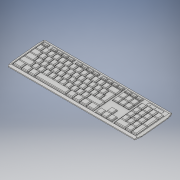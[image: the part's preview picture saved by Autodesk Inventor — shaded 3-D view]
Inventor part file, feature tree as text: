
AUTODESK INVENTOR PART (.ipt)
format: ipt  version: 2017 (Build 210142000, 142)  size: 3,176,448 bytes
history: native  units: in
note: dims shown in document units (in); Inventor stores cm internally (conversion verified against a paired STEP export)
features: other x111, loft x104, extrude x17, sketch x15, mirror x3, plane x2, fillet x1
ambient origin geometry x8: Origin, YZ Plane, XZ Plane, XY Plane, X Axis, Y Axis, Z Axis, Center Point
bodies: Solid4 (feature_tree)
feature tree (253):
  other  "key board"
  extrude  "key board to cut from"  Depth=0.4271in
  extrude  "curve top and bottom"  Depth=0.0938in
  extrude  "curve corners"  Depth=0.3125in
  other  "side curve workplane"
  extrude  "right curve edge"  Depth=0.0053in
  mirror  "mirror plane"
  mirror  "mirror right edge"
  other  "right curve workplane"
  extrude  "right curve diaganal"  Depth=0.0163in
  mirror  "mirror curve right"
  extrude  "leftover from diaganal and right curve"  Depth=0.0238in
  extrude  "back curve corner"  Depth=0.009in
  extrude  "ramp for keys"  Depth=0.0011in
  other  "ramp flushing plane"
  extrude  "ramp flushed"  Depth=0.015in
  extrude  "ramp random extion"  Depth=0.0153in
  plane  "Work Plane9"
  extrude  "top side curve"  Depth=1.0in TaperAngle=0.0deg
  extrude  "key slots"  Depth=0.0208in
  other  "keys workplane"
  extrude  "bottom of keys"  Depth=0.0036in
  plane  "Work Plane10"
  sketch  "Sketch23"  dims[d45=90.0deg d55=0.0208in]
  extrude  "Caps lock and Num Lock light indicators cut out"  Depth=1.0in TaperAngle=0.0deg
  sketch  "Sketch25"  dims[d58=0.7136in d67=1.0in d68=0.0in]
  extrude  "light indicators cut out"  Depth=0.0036in
  extrude  "light indicators join"  Depth=0.0005in TaperAngle=0.0deg
  loft  "~ key"
  loft  "1! key"
  loft  "2@ key"
  loft  "3# key"
  loft  "4$ key"
  loft  "5% key"
  loft  "6^ key"
  loft  "7& key"
  loft  "8* key"
  loft  "9( key"
  loft  "0) key"
  loft  "-_ key"
  loft  "=+ key"
  loft  "Q key"
  loft  "W key"
  loft  "E key"
  loft  "R key"
  loft  "T key"
  loft  "Y key"
  loft  "U key"
  loft  "I key"
  loft  "O key"
  loft  "P key"
  loft  "[{ key"
  loft  "]} key"
  loft  "\| key"
  loft  "'" key"
  loft  ";: key"
  loft  "L key"
  loft  "K key"
  loft  "J key"
  loft  "H key"
  loft  "G key"
  loft  "F key"
  loft  "D key"
  loft  "S key"
  loft  "A key"
  loft  "Z key"
  loft  "X key"
  loft  "C key"
  loft  "V key"
  loft  "B key"
  loft  "N key"
  loft  "M key"
  loft  ",< key"
  loft  ".> key"
  loft  "/? key"
  loft  "Tab  key"
  loft  "Caps Lock  key"
  loft  "Left Shift key"
  loft  "Left Ctrl key"
  loft  "Left FN  key"
  loft  "Left Alt"
  loft  "space bar key"
  loft  "Right Alt  key"
  loft  "Windows  key"
  loft  "Menu  key"
  loft  "Right Ctrl  key"
  loft  "Right Shift  key"
  loft  "Enter  key"
  loft  "Backspace  key"
  loft  "Esc  key"
  loft  "F1  key"
  loft  "F2  key"
  loft  "F3  key"
  loft  "F4  key"
  loft  "F5  key"
  loft  "F6 key"
  loft  "F7 key"
  loft  "F8 key"
  loft  "F9 key"
  loft  "F10  key"
  loft  "F11  key"
  loft  "F12  key"
  loft  "Print Screen  key"
  loft  "Scroll Lock  key"
  loft  "Pause Break  key"
  loft  "Insert  key"
  loft  "Delete  key"
  loft  "End  key"
  loft  "Home  key"
  loft  "Page UP  key"
  loft  "Page Down  key"
  loft  "Up Arrow  key"
  loft  "Left Arrow  key"
  loft  "Down Arrow  key"
  loft  "Right Arrow  key"
  loft  "Num Lock  key"
  loft  "Num /  key"
  loft  "Num *  key"
  loft  "Num -  key"
  loft  "Num +  key"
  loft  "Num Enter  key"
  loft  "Num .  key"
  loft  "Num 1  key"
  loft  "Num 2  key"
  loft  "Num 3  key"
  loft  "Num 4  key"
  loft  "Num 5  key"
  extrude  "little knobs for blind"  Depth=0.1063in
  fillet  "Fillet little knobs"  Radius=0.0041in
  loft  "Num 6  key"
  loft  "Num 7  key"
  loft  "Num 8  key"
  loft  "Num 9  key"
  loft  "Num 0  key"
  other  "put in middle of terminal"
  other  "middle of the key board front to back"
  sketch  "Sketch3"  dims[d12=1.4896in d13=0.4271in]
  sketch  "Sketch4"  dims[d14=0.0749in d15=0.0in d16=0.0938in]
  sketch  "Sketch5"  dims[d17=0.032in d18=0.3125in]
  sketch  "Sketch6"  dims[d19=0.0053in d20=0.0053in]
  sketch  "Sketch8"  dims[d22=0.0036in d23=0.0163in]
  sketch  "Sketch15"  dims[d25=0.0238in d29=0.0238in]
  sketch  "Sketch16"  dims[d30=0.032in d32=0.009in]
  sketch  "Sketch18"  dims[d33=0.0092in d34=0.0011in]
  sketch  "Sketch19"  dims[d36=1.0in d37=0.0in d39=0.015in]
  sketch  "Sketch21"  dims[d40=0.0666in d41=0.0153in]
  sketch  "Sketch22"  dims[d42=0.0621in d43=1.0in d44=0.0in]
  other  "Edges1"
  other  "Edges2"
  other  "Edges3"
  other  "Edges4"
  other  "Edges5"
  other  "Edges6"
  other  "Edges7"
  other  "Edges8"
  other  "Edges9"
  other  "Edges10"
  other  "Edges11"
  other  "Edges12"
  other  "Edges13"
  other  "Edges14"
  other  "Edges15"
  other  "Edges16"
  other  "Edges17"
  other  "Edges18"
  other  "Edges19"
  other  "Edges20"
  other  "Edges21"
  other  "Edges22"
  other  "Edges23"
  other  "Edges24"
  other  "Edges25"
  other  "Edges26"
  other  "Edges27"
  other  "Edges28"
  other  "Edges29"
  other  "Edges30"
  other  "Edges31"
  other  "Edges32"
  other  "Edges33"
  other  "Edges34"
  other  "Edges35"
  other  "Edges36"
  other  "Edges37"
  other  "Edges38"
  other  "Edges39"
  other  "Edges40"
  other  "Edges41"
  other  "Edges42"
  other  "Edges43"
  other  "Edges44"
  other  "Edges45"
  other  "Edges46"
  other  "Edges47"
  other  "Edges48"
  other  "Edges49"
  other  "Edges50"
  other  "Edges51"
  other  "Edges52"
  other  "Edges53"
  other  "Edges54"
  other  "Edges55"
  other  "Edges56"
  other  "Edges57"
  other  "Edges58"
  other  "Edges59"
  other  "Edges60"
  other  "Edges61"
  other  "Edges62"
  other  "Edges63"
  other  "Edges64"
  other  "Edges65"
  other  "Edges66"
  other  "Edges67"
  other  "Edges68"
  other  "Edges69"
  other  "Edges70"
  other  "Edges71"
  other  "Edges72"
  other  "Edges73"
  other  "Edges74"
  other  "Edges75"
  other  "Edges76"
  other  "Edges77"
  other  "Edges78"
  other  "Edges79"
  other  "Edges80"
  other  "Edges81"
  other  "Edges82"
  other  "Edges83"
  other  "Edges84"
  other  "Edges85"
  other  "Edges86"
  other  "Edges87"
  other  "Edges88"
  other  "Edges89"
  other  "Edges90"
  other  "Edges91"
  other  "Edges92"
  other  "Edges93"
  other  "Edges94"
  other  "Edges95"
  other  "Edges96"
  other  "Edges97"
  other  "Edges98"
  other  "Edges99"
  other  "Edges100"
  other  "Edges101"
  other  "Edges102"
  other  "Edges103"
  other  "Edges104"
  sketch  "Sketch24"  dims[d56=0.0053in d57=0.0036in]
  sketch  "Sketch26"  dims[d73=0.0053in d74=0.0036in d76=1.0in d77=0.0in d78=1.0in d79=0.0in d81=0.0058in d82=0.0058in d90=0.0307in d91=0.0307in d94=0.017in d95=0.0653in d96=0.0653in d97=0.0653in d98=0.0653in d99=0.0653in d100=0.017in d101=0.1958in d102=0.1305in d104=0.3262in d106=0.0746in d108=0.0083in d109=0.261in d111=0.0262in d112=0.261in d113=0.0262in d114=0.261in d115=0.02in d116=0.0in d117=0.0083in d118=0.0592in d119=0.0592in d120=0.0592in d121=0.0592in d122=0.0592in d123=0.0592in d124=0.0592in d125=0.0592in d126=0.0592in d127=0.0592in d128=0.0592in d129=0.0592in d130=0.0592in d131=0.0592in d132=0.0041in d133=0.0041in d134=0.0041in d135=0.0041in d136=0.0041in d137=0.0041in d138=0.0041in d139=0.0041in d146=0.0592in d147=0.0592in d148=0.0592in d149=0.0592in d150=0.0592in d151=0.0592in d152=0.0592in d153=0.0592in d154=0.0592in d155=0.0592in d156=0.0592in d157=0.0592in d160=0.0041in d161=0.0041in d162=0.0041in d163=0.0041in d164=0.0041in d166=0.0041in d167=0.0041in d172=0.0041in d173=0.032in d174=0.017in d175=1.0in d176=0.0in d177=0.066in d178=0.066in d179=0.0686in d180=0.0686in d183=90.0deg d184=1.0in d185=0.0in d186=0.0328in d187=0.0031in d188=0.0031in d189=0.063in d190=0.0328in d191=0.0031in d192=0.0031in d193=0.063in d194=1.0in d195=0.0in d196=0.0041in d197=0.1095in d198=0.0041in d199=0.0041in d200=0.0041in d201=0.0041in d202=0.0041in d203=0.0041in d204=0.0041in d205=0.0592in d206=0.0592in d207=0.0592in d208=0.0592in d209=0.0041in d210=0.0041in d213=0.0304in d214=90.0deg d215=0.0091in d216=0.0249in d217=0.0091in d218=0.0249in d219=1.0in d220=0.0in d222=0.0041in d226=0.0592in d227=0.0592in d228=0.0592in d229=0.0592in d230=0.0041in d231=0.0041in d232=0.0041in d233=0.0041in d234=0.0592in d235=0.0041in d236=0.0041in d237=0.0041in d238=0.0592in d239=0.0592in d240=0.0592in d241=0.0592in d242=0.0041in d243=0.0041in d244=0.0041in d248=0.0592in d249=0.0041in d250=0.0041in d251=0.0041in d252=0.0041in d253=0.0041in d254=0.1958in d255=0.017in d256=0.0592in d257=0.0592in d258=0.0592in d260=0.0041in d261=0.0041in d263=0.0592in d264=0.0041in d265=0.0041in d267=0.0592in d268=0.0592in d269=0.0592in d270=0.0592in d271=0.0592in d272=0.0592in d273=0.0592in d274=0.0592in d275=0.0592in d276=0.0592in d277=0.0592in d278=0.0592in d279=0.0592in d280=0.0592in d281=0.0041in d282=0.0041in d283=0.0041in d284=0.0041in d285=0.0041in d286=0.0041in d287=0.0592in d288=0.0592in d289=0.0592in d290=0.0592in d291=0.0592in d292=0.0592in d293=0.0592in d294=0.0592in d295=0.0592in d296=0.0592in d297=0.0041in d298=0.0041in d299=0.0041in d300=0.0041in d301=0.0041in d302=0.0041in d303=0.0041in d304=0.0592in d305=0.0041in d306=0.0041in d307=0.0902in d308=0.0592in d310=0.0041in d311=0.0592in d312=0.1063in d313=0.0041in d314=0.0592in d315=0.0592in d316=0.0592in d317=0.0592in d318=0.0592in d319=0.0592in d320=0.0592in d321=0.0592in d322=0.0592in d323=0.0592in d324=0.0592in d325=0.0592in d326=0.0592in d327=0.0592in d328=0.0041in d329=0.0041in d330=0.0041in d331=0.0041in d332=0.0041in d333=0.0041in d334=0.0592in d335=0.0592in d336=0.0592in d337=0.0592in d338=0.0592in d339=0.0592in d340=0.0592in d341=0.0592in d342=0.0592in d343=0.0592in d344=0.0041in d345=0.0041in d346=0.0041in d347=0.0041in d348=0.0041in d349=0.0592in d350=0.0041in d351=0.0041in d352=0.0041in d353=0.0041in d354=0.0592in d355=0.0592in d356=0.0592in d357=0.0592in d358=0.0592in d359=0.0592in d360=0.0592in d361=0.0592in d362=0.0592in d363=0.0592in d364=0.0592in d365=0.0592in d366=0.0592in d367=0.0592in d368=0.0041in d369=0.0041in d370=0.0041in d371=0.0041in d372=0.0041in d373=0.0041in d374=0.0592in d375=0.0592in d376=0.0592in d377=0.0592in d378=0.0592in d379=0.0592in d380=0.0041in d381=0.0041in d382=0.0041in d383=0.0592in d384=0.0041in d385=0.0041in d386=0.0592in d387=0.0041in d388=0.1355in d389=0.0041in d392=0.0041in d393=0.0592in d394=0.0899in d395=0.0041in d396=0.0041in d397=0.0041in d398=0.0041in d399=0.0041in d400=0.0041in d401=0.0747in d402=0.0747in d403=0.3529in d404=0.0743in d405=0.0755in d406=0.0041in d407=0.0041in d408=0.0747in d410=0.0592in d411=0.0592in d412=0.0592in d413=0.0592in d414=0.0041in d415=0.0592in d416=0.0041in d417=0.0592in d418=0.0592in d419=0.0592in d420=0.0592in d421=0.0041in d422=0.0592in d423=0.0041in d424=0.0592in d425=0.0592in d426=0.0592in d427=0.0592in d428=0.0041in d429=0.0592in d430=0.0041in d431=0.0592in d432=0.0592in d433=0.0592in d434=0.0592in d435=0.0041in d436=0.0592in d437=0.0041in d438=0.0592in d439=0.0592in d440=0.0592in d441=0.0592in d442=0.0041in d443=0.0592in d444=0.0041in d445=0.0592in d446=0.0592in d447=0.0592in d448=0.0592in d449=0.0041in d450=0.0592in d451=0.0041in d452=0.0592in d453=0.0592in d454=0.0592in d455=0.0592in d456=0.0041in d457=0.0592in d458=0.0041in d459=0.0592in d460=0.0592in d461=0.0592in d462=0.0592in d463=0.0041in d464=0.0592in d465=0.0041in d466=0.0041in d467=0.0041in d468=0.0041in d469=0.0041in d470=0.0041in d471=0.0041in d472=0.0041in d473=0.0041in d474=0.0041in d475=0.0041in d476=0.0041in d477=0.0592in d478=0.0592in d479=0.0592in d480=0.0592in d481=0.0592in d482=0.0592in d483=0.0592in d484=0.0592in d485=0.0592in d486=0.0592in d487=0.0592in d488=0.0592in d489=0.0041in d490=0.0041in d491=0.0041in d492=0.0041in d495=0.032in d496=0.0592in d497=0.0592in d498=0.0592in d499=0.0592in d500=0.0592in d501=0.0592in d502=0.0041in d503=0.0041in d504=0.0592in d505=0.0592in d506=0.0592in d507=0.0592in d508=0.0592in d509=0.0592in d510=0.0041in d512=0.0208in d513=0.0091in d514=1.0in d515=0.0in d516=0.0592in d517=0.0592in d518=0.0592in d519=0.0592in d520=0.0592in d522=0.0592in d523=0.0592in d525=0.0592in d526=0.0592in d527=0.0592in d528=0.0592in d530=0.0592in d531=0.0592in d533=0.0592in d534=0.0592in d535=0.0592in d536=0.0592in d538=0.0592in d540=0.0134in d541=0.0in d542=0.0083in d901=0.0246in d905=0.0271in d906=0.021in d909=0.0246in d910=0.0271in d911=0.021in d912=0.0592in d1093=0.0246in d1094=0.0271in d1095=0.021in d1096=0.0592in d1097=0.0246in d1098=0.0271in d1099=0.021in d1100=0.0592in d1101=0.0246in d1102=0.0271in d1103=0.021in d1104=0.0592in d1105=0.0246in d1106=0.0271in d1107=0.021in d1108=0.0592in d1109=0.0246in d1110=0.0271in d1111=0.021in d1112=0.0592in d1113=0.0246in d1114=0.0271in d1115=0.021in d1116=0.0592in d1117=0.0246in d1118=0.0271in d1119=0.021in d1120=0.0592in d1121=0.0246in d1122=0.0271in d1123=0.021in d1124=0.0592in d1125=0.0246in d1126=0.0271in d1127=0.021in d1128=0.0592in d1129=0.0246in d1130=0.0271in d1131=0.021in d1132=0.0592in d1133=0.0246in d1134=0.0271in d1135=0.021in d1136=0.0592in d1137=0.0246in d1138=0.0271in d1139=0.021in d1140=0.0592in d1141=0.0246in d1142=0.0271in d1143=0.021in d1144=0.0592in d1145=0.0246in d1146=0.0271in d1147=0.021in d1148=0.0592in d1149=0.0246in d1150=0.0271in d1151=0.021in d1152=0.0592in d1153=0.0246in d1154=0.0271in d1155=0.021in d1156=0.0592in d1157=0.0246in d1158=0.0271in d1159=0.021in d1160=0.0592in d1161=0.0246in d1162=0.0271in d1163=0.021in d1164=0.0592in d1165=0.0246in d1166=0.0271in d1167=0.021in d1168=0.0592in d1169=0.0246in d1170=0.0271in d1171=0.021in d1172=0.0592in d1173=0.0246in d1174=0.0271in d1175=0.021in d1176=0.0592in d1177=0.0246in d1178=0.0271in d1179=0.021in d1180=0.0592in d1181=0.0246in d1182=0.0271in d1183=0.021in d1184=0.0592in d1185=0.0246in d1186=0.0271in d1187=0.021in d1188=0.0592in d1189=0.0246in d1190=0.0271in d1191=0.021in d1192=0.0592in d1193=0.0246in d1194=0.0271in d1195=0.021in d1196=0.0592in d1197=0.0246in d1198=0.0271in d1199=0.021in d1200=0.0592in d1201=0.0246in d1202=0.0271in d1203=0.021in d1204=0.0592in d1205=0.0246in d1206=0.0271in d1207=0.021in d1208=0.0592in d1209=0.0246in d1210=0.0271in d1211=0.021in d1212=0.0592in d1213=0.0246in d1214=0.0271in d1215=0.021in d1216=0.0592in d1217=0.0246in d1218=0.0271in d1219=0.021in d1220=0.0592in d1221=0.0246in d1222=0.0271in d1223=0.021in d1224=0.0592in d1225=0.0246in d1226=0.0271in d1227=0.021in d1228=0.0592in d1229=0.0246in d1230=0.0271in d1231=0.021in d1232=0.0592in d1233=0.0246in d1234=0.0271in d1235=0.021in d1236=0.0592in d1237=0.0246in d1238=0.0271in d1239=0.021in d1240=0.0592in d1241=0.0246in d1242=0.0271in d1243=0.021in d1244=0.0592in d1245=0.0246in d1246=0.0271in d1247=0.021in d1248=0.0592in d1249=0.0246in d1250=0.0271in d1251=0.021in d1252=0.0592in d1253=0.0246in d1254=0.0271in d1255=0.021in d1256=0.0592in d1257=0.0246in d1258=0.0271in d1259=0.021in d1260=0.0592in d1261=0.0246in d1262=0.0271in d1263=0.021in d1264=0.0592in d1265=0.0246in d1266=0.0271in d1267=0.021in d1268=0.0592in d1269=0.0246in d1270=0.0271in d1271=0.021in d1272=0.0592in d1273=0.0in d1274=90.0deg d1275=0.0in d1276=90.0deg d1277=0.0in d1278=90.0deg d1279=0.0in d1280=90.0deg d1281=0.0in d1282=90.0deg d1283=0.0in d1284=90.0deg d1285=0.0in d1286=90.0deg d1287=0.0in d1288=90.0deg d1289=0.0in d1290=90.0deg d1291=0.0in d1292=90.0deg d1293=0.0in d1294=90.0deg d1295=0.0in d1296=90.0deg d1297=0.0in d1298=90.0deg d1299=0.0in d1300=90.0deg d1301=0.0in d1302=90.0deg d1303=0.0in d1304=90.0deg d1305=0.0in d1306=90.0deg d1307=0.0in d1308=90.0deg d1309=0.0in d1310=90.0deg d1311=0.0in d1312=90.0deg d1313=0.0in d1314=90.0deg d1315=0.0in d1316=90.0deg d1317=0.0in d1318=90.0deg d1319=0.0in d1320=90.0deg d1321=0.0in d1322=90.0deg d1323=0.0in d1324=90.0deg d1325=0.0in d1326=90.0deg d1327=0.0in d1328=90.0deg d1329=0.0in d1330=90.0deg d1331=0.0in d1332=90.0deg d1333=0.0in d1334=90.0deg d1335=0.0in d1336=90.0deg d1337=0.0in d1338=90.0deg d1339=0.0in d1340=90.0deg d1341=0.0in d1342=90.0deg d1343=0.0in d1344=90.0deg d1345=0.0in d1346=90.0deg d1347=0.0in d1348=90.0deg d1349=0.0in d1350=90.0deg d1351=0.0in d1352=90.0deg d1353=0.0in d1354=90.0deg d1355=0.0in d1356=90.0deg d1357=0.0in d1358=90.0deg d1359=0.0in d1360=90.0deg d1361=0.0in d1362=90.0deg d1363=0.0in d1364=90.0deg d1365=0.0in d1366=90.0deg d1367=0.0in d1368=90.0deg d1369=0.0in d1370=90.0deg d1371=0.0in d1372=90.0deg d1373=0.0in d1374=90.0deg d1375=0.0in d1376=90.0deg d1377=0.0in d1378=90.0deg d1379=0.0in d1380=90.0deg d1381=0.0in d1382=90.0deg d1383=0.0in d1384=90.0deg d1385=0.0in d1386=90.0deg d1387=0.0in d1388=90.0deg d1389=0.0in d1390=90.0deg d1391=0.0in d1392=90.0deg d1393=0.0in d1394=90.0deg d1395=0.0in d1396=90.0deg d1397=0.0in d1398=90.0deg d1399=0.0in d1400=90.0deg d1401=0.0in d1402=90.0deg d1403=0.0in d1404=90.0deg d1405=0.0in d1406=90.0deg d1407=0.0in d1408=90.0deg d1409=0.0in d1410=90.0deg d1411=0.0in d1412=90.0deg d1413=0.0in d1414=90.0deg d1415=0.0in d1416=90.0deg d1417=0.0in d1418=90.0deg d1419=0.0in d1420=90.0deg d1421=0.0in d1422=90.0deg d1423=0.0in d1424=90.0deg d1425=0.0in d1426=90.0deg d1427=0.0in d1428=90.0deg d1429=0.0in d1430=90.0deg d1431=0.0in d1432=90.0deg d1433=0.0in d1434=90.0deg d1435=0.0in d1436=90.0deg d1437=0.0in d1438=90.0deg d1439=0.0in d1440=90.0deg d1441=0.0in d1442=90.0deg d1443=0.0in d1444=90.0deg d1445=0.0in d1446=90.0deg d1447=0.0in d1448=90.0deg d1449=0.0in d1450=90.0deg d1451=0.0in d1452=90.0deg d1453=0.0in d1454=90.0deg d1455=0.0in d1456=90.0deg d1457=0.0in d1458=90.0deg d1459=0.0in d1460=90.0deg d1463=0.0246in d1464=0.0271in d1465=0.0365in d1466=0.0592in d1467=0.0246in d1468=0.0271in d1469=0.0445in d1470=0.0592in d1471=0.0902in d1473=0.0246in d1474=0.0271in d1475=0.0591in d1476=0.0592in d1477=0.1063in d1479=0.0246in d1480=0.0271in d1481=0.0461in d1482=0.0592in d1484=0.0246in d1485=0.0271in d1486=0.0363in d1487=0.0592in d1488=0.1355in d1489=0.0246in d1490=0.0271in d1491=0.0287in d1492=0.0592in d1493=0.0899in d1494=0.0246in d1495=0.0271in d1496=0.0288in d1497=0.0592in d1498=0.0899in d1499=0.0246in d1500=0.0271in d1501=0.1678in d1502=0.0592in d1503=0.0899in d1504=0.0246in d1505=0.0271in d1506=0.0285in d1507=0.0592in d1508=0.0899in d1509=0.0246in d1510=0.0271in d1511=0.0291in d1512=0.0592in d1513=0.0899in d1514=0.0246in d1515=0.0271in d1516=0.0288in d1517=0.0592in d1518=0.0899in d1519=0.0246in d1520=0.0271in d1521=0.0348in d1522=0.0592in d1523=0.0899in d1524=0.0246in d1525=0.0271in d1526=0.0713in d1527=0.0592in d1528=0.0899in d1529=0.0869in d1530=0.1598in d1532=0.0271in d1533=0.0306in d1534=0.0592in d1535=0.0246in d1538=0.0592in d1539=0.0785in d1540=0.0624in d1541=0.0226in d1542=0.0in d1543=90.0deg d1544=0.0in d1545=90.0deg d1546=0.0in d1547=90.0deg d1548=0.0in d1549=90.0deg d1550=0.0in d1551=90.0deg d1552=0.0in d1553=90.0deg d1554=0.0in d1555=90.0deg d1556=0.0in d1557=90.0deg d1558=0.0in d1559=90.0deg d1560=0.0in d1561=90.0deg d1562=0.0in d1563=90.0deg d1564=0.0in d1565=90.0deg d1566=0.0in d1567=90.0deg d1568=0.0in d1569=90.0deg d1570=0.0in d1571=90.0deg d1572=0.0in d1573=90.0deg d1574=0.0in d1575=90.0deg d1576=0.0in d1577=90.0deg d1578=0.0in d1579=90.0deg d1580=0.0in d1581=90.0deg d1582=0.0in d1583=90.0deg d1584=0.0in d1585=90.0deg d1586=0.0in d1587=90.0deg d1588=0.0in d1589=90.0deg d1590=0.0in d1591=90.0deg d1592=0.0in d1593=90.0deg d1594=0.0in d1595=90.0deg d1596=0.0in d1597=90.0deg d1598=0.0664in d1599=0.0251in d1602=0.0101in d1603=0.0076in d1604=0.0246in d1605=0.0101in d1606=0.0076in d1607=0.0246in d1608=0.0251in d1609=0.0664in d1610=0.0101in d1611=0.0076in d1612=0.0246in d1613=0.0251in d1614=0.0664in d1615=0.0101in d1616=0.0076in d1617=0.0246in d1618=0.0251in d1619=0.0664in d1620=0.0101in d1621=0.0076in d1622=0.0246in d1623=0.0251in d1624=0.0664in d1625=0.0101in d1626=0.0076in d1627=0.0246in d1628=0.0251in d1629=0.0664in d1630=0.0101in d1631=0.0076in d1632=0.0246in d1633=0.0251in d1634=0.0664in d1635=0.0101in d1636=0.0076in d1637=0.0246in d1638=0.0251in d1639=0.0664in d1640=0.0101in d1641=0.0076in d1642=0.0246in d1643=0.0251in d1644=0.0664in d1645=0.0101in d1646=0.0076in d1647=0.0246in d1648=0.0251in d1649=0.0664in d1650=0.0101in d1651=0.0076in d1652=0.0246in d1653=0.0251in d1654=0.0664in d1655=0.0101in d1656=0.0076in d1657=0.0246in d1658=0.0251in d1659=0.0664in d1660=0.0101in d1661=0.0076in d1662=0.0246in d1663=0.0251in d1664=0.0664in d1665=0.0101in d1666=0.0076in d1667=0.0246in d1668=0.0251in d1669=0.0664in d1670=0.0101in d1671=0.0076in d1672=0.0246in d1673=0.0251in d1674=0.0664in d1675=0.0101in d1676=0.0076in d1677=0.0246in d1678=0.0251in d1679=0.0664in d1680=0.0in d1681=90.0deg d1682=0.0in d1683=90.0deg d1684=0.0in d1685=90.0deg d1686=0.0in d1687=90.0deg d1688=0.0in d1689=90.0deg d1690=0.0in d1691=90.0deg d1692=0.0in d1693=90.0deg d1694=0.0in d1695=90.0deg d1696=0.0in d1697=90.0deg d1698=0.0in d1699=90.0deg d1700=0.0in d1701=90.0deg d1702=0.0in d1703=90.0deg d1704=0.0in d1705=90.0deg d1706=0.0in d1707=90.0deg d1708=0.0in d1709=90.0deg d1710=0.0in d1711=90.0deg d1712=0.0in d1713=90.0deg d1714=0.0in d1715=90.0deg d1716=0.0in d1717=90.0deg d1718=0.0in d1719=90.0deg d1720=0.0in d1721=90.0deg d1722=0.0in d1723=90.0deg d1724=0.0in d1725=90.0deg d1726=0.0in d1727=90.0deg d1728=0.0in d1729=90.0deg d1730=0.0in d1731=90.0deg d1732=0.0in d1733=90.0deg d1734=0.0in d1735=90.0deg d1736=0.0in d1737=90.0deg d1738=0.0in d1739=90.0deg d1740=0.0in d1741=90.0deg d1742=0.0in d1743=90.0deg d1744=0.0271in d1745=0.0246in d1746=0.0246in d1747=0.0251in d1748=0.0664in d1749=0.0271in d1750=0.0246in d1751=0.0246in d1752=0.0251in d1753=0.0664in d1754=0.0271in d1755=0.0246in d1756=0.0246in d1757=0.0251in d1758=0.0664in d1759=0.0271in d1760=0.0246in d1761=0.0246in d1762=0.0251in d1763=0.0664in d1764=0.0271in d1765=0.0246in d1766=0.0246in d1767=0.0251in d1768=0.0664in d1769=0.0271in d1770=0.0246in d1771=0.0246in d1772=0.0251in d1773=0.0664in d1774=0.0271in d1775=0.0246in d1776=0.0246in d1777=0.0592in d1778=0.0664in d1779=0.0592in d1780=0.0271in d1781=0.0246in d1782=0.0246in d1783=0.0592in d1784=0.0664in d1785=0.0592in d1792=0.0271in d1793=0.0246in d1794=0.0246in d1795=0.0592in d1796=0.0664in d1797=0.0592in d1798=0.0271in d1799=0.0246in d1800=0.021in d1801=0.0592in d1802=0.0664in d1803=0.0592in d1804=0.0271in d1805=0.0246in d1806=0.021in d1807=0.0592in d1808=0.0664in d1809=0.0592in d1810=0.0271in d1811=0.0246in d1812=0.021in d1813=0.0592in d1814=0.0664in d1815=0.0592in d1816=0.0271in d1817=0.0246in d1818=0.021in d1819=0.0592in d1820=0.0664in d1821=0.0592in d1822=0.0271in d1823=0.0246in d1824=0.021in d1825=0.0592in d1826=0.0664in d1827=0.0592in d1828=0.0271in d1829=0.0246in d1830=0.021in d1831=0.0592in d1832=0.0664in d1833=0.0592in d1834=0.0271in d1835=0.0246in d1836=0.021in d1837=0.0592in d1838=0.0664in d1839=0.0592in d1840=0.0271in d1841=0.0246in d1842=0.021in d1843=0.0592in d1844=0.0664in d1845=0.0592in d1846=0.0271in d1847=0.0246in d1848=0.021in d1849=0.0592in d1850=0.0664in d1851=0.0592in d1852=0.0271in d1853=0.0246in d1854=0.021in d1855=0.0592in d1856=0.0664in d1857=0.0592in d1858=0.0271in d1859=0.0246in d1860=0.021in d1861=0.0592in d1862=0.0664in d1863=0.0592in d1864=0.0271in d1865=0.0246in d1866=0.021in d1867=0.0592in d1868=0.0664in d1869=0.0592in d1870=0.0271in d1871=0.0246in d1872=0.021in d1873=0.0592in d1874=0.0664in d1875=0.0592in d1876=0.0271in d1877=0.0246in d1878=0.0246in d1879=0.0592in d1880=0.0664in d1881=0.0592in d1882=0.0271in d1883=0.0246in d1884=0.0246in d1885=0.0592in d1886=0.0664in d1887=0.0592in d1888=0.0271in d1889=0.0246in d1890=0.0526in d1891=0.0592in d1892=0.0664in d1893=0.0592in d1900=0.0588in d1901=0.0563in d1902=0.021in d1903=0.0592in d1904=0.0664in d1905=0.0592in d1912=0.1225in d1913=0.1225in d1914=0.1225in d1915=0.0588in d1916=0.0563in d1917=0.021in d1918=0.0592in d1919=0.0592in d1920=0.0592in d1921=0.0592in d1922=0.0in d1923=90.0deg d1924=0.0in d1925=90.0deg d1926=0.0in d1927=90.0deg d1928=0.0in d1929=90.0deg d1930=0.0in d1931=90.0deg d1932=0.0in d1933=90.0deg d1934=0.0in d1935=90.0deg d1936=0.0in d1937=90.0deg d1938=0.0in d1939=90.0deg d1940=0.0in d1941=90.0deg d1942=0.0in d1943=90.0deg d1944=0.0in d1945=90.0deg d1946=0.0in d1947=90.0deg d1948=0.0in d1949=90.0deg d1950=0.0in d1951=90.0deg d1952=0.0in d1953=90.0deg d1954=0.0in d1955=90.0deg d1956=0.0in d1957=90.0deg d1958=0.0in d1959=90.0deg d1960=0.0in d1961=90.0deg d1962=0.0in d1963=90.0deg d1964=0.0in d1965=90.0deg d1966=0.0in d1967=90.0deg d1968=0.0in d1969=90.0deg d1970=0.0in d1971=90.0deg d1972=0.0in d1973=90.0deg d1974=0.0in d1975=90.0deg d1976=0.0in d1977=90.0deg d1978=0.0in d1979=90.0deg d1980=0.0in d1981=90.0deg d1982=0.0in d1983=90.0deg d1984=0.0in d1985=90.0deg d1986=0.0in d1987=90.0deg d1988=0.0in d1989=90.0deg d1990=0.0in d1991=90.0deg d1992=0.0in d1993=90.0deg d1994=0.0in d1995=90.0deg d1996=0.0in d1997=90.0deg d1998=0.0in d1999=90.0deg d2000=0.0in d2001=90.0deg d2002=0.0in d2003=90.0deg d2004=0.0in d2005=90.0deg d2006=0.0in d2007=90.0deg d2008=0.0in d2009=90.0deg d2010=0.0in d2011=90.0deg d2012=0.0in d2013=90.0deg d2014=0.0in d2015=90.0deg d2016=0.0in d2017=90.0deg d2018=0.0in d2019=90.0deg d2020=0.0in d2021=90.0deg d2022=0.0in d2023=90.0deg d2024=0.0in d2025=90.0deg d2026=0.0in d2027=90.0deg d2028=0.0in d2029=90.0deg d2033=0.0325in d2035=0.0023in d2036=0.0023in d2037=0.088in d2038=0.0581in d2039=0.0287in d2040=0.0073in d2041=0.0592in d2042=0.0013in d2043=0.0in d2044=0.0592in d2045=0.0073in d2046=0.0287in d2047=0.0013in d2048=0.0in d2049=0.0013in d2050=0.0in d2057=0.0067in d2061=0.0015in d2062=0.0112in d2063=0.0015in d2064=0.0112in d2065=0.0015in d2066=0.0112in d2067=0.0067in d2068=0.0067in d2069=0.0018in d2070=0.0in d2071=0.0005in]
